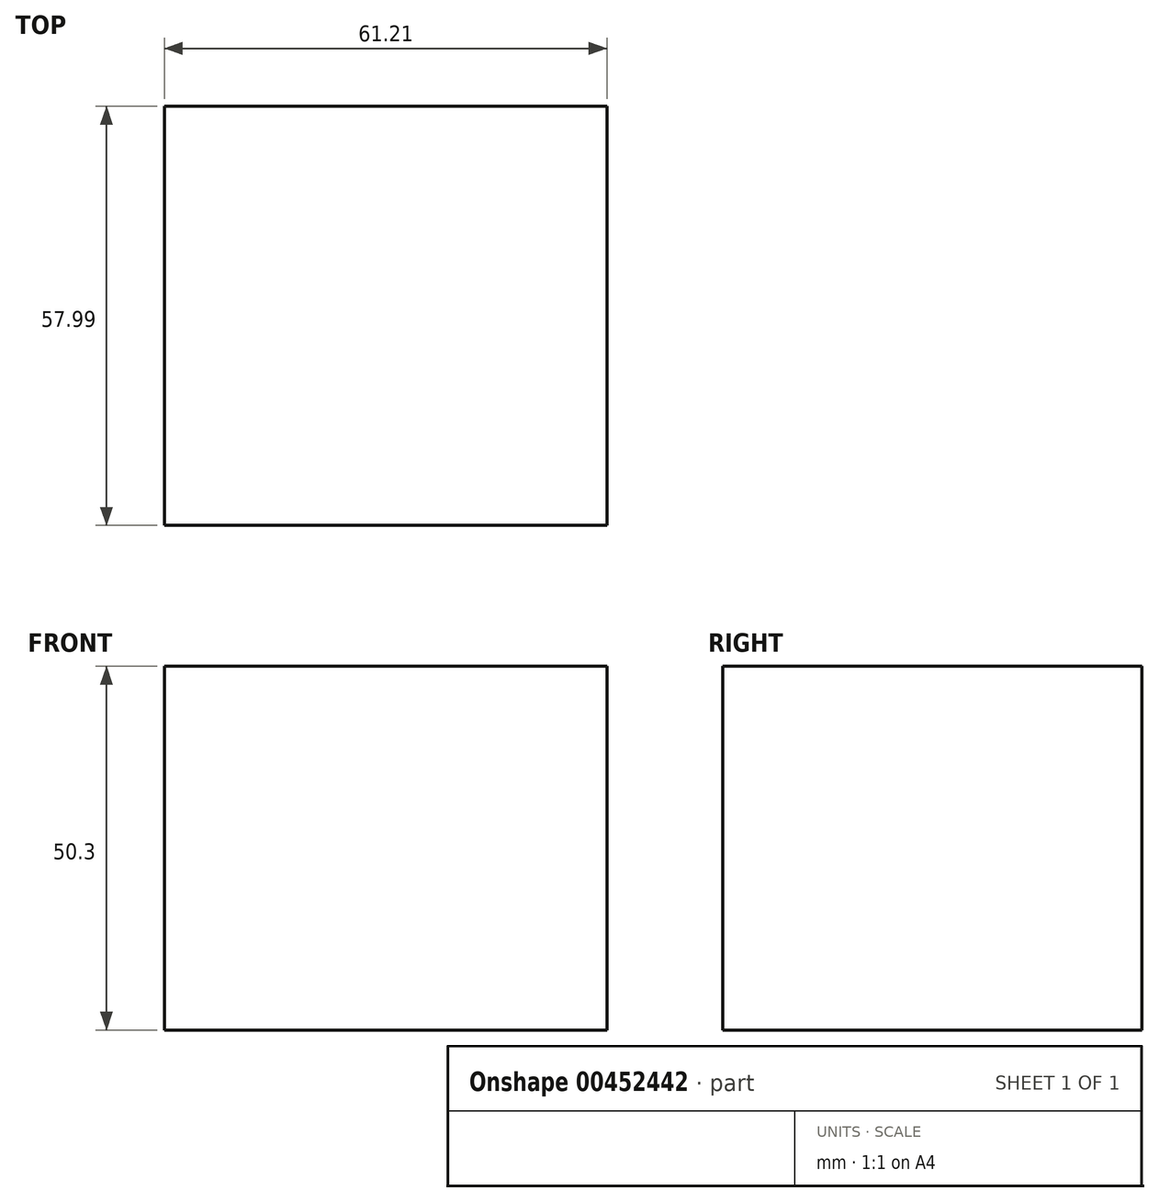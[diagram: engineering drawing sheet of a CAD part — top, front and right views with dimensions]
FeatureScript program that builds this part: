
annotation { "Feature Type Name" : "Feature", "Feature Type Description" : "" }
export const myFeature = defineFeature(function(context is Context, id is Id, definition is map)
    precondition{}
    {
        {
            var Q0;
            Q0=qCreatedBy(makeId("Right.planeOp"),FACE);
            var sketch = newSketch(context, id + "F0", { "sketchPlane" : qUnion([Q0])});
            skLineSegment(sketch, "E0.bottom", {"start": v(0, 0) * mm, "end": v(57.99, 0) * mm});
            skLineSegment(sketch, "E0.top", {"start": v(0, -50.3) * mm, "end": v(57.99, -50.3) * mm});
            skLineSegment(sketch, "E0.left", {"start": v(0, 0) * mm, "end": v(0, -50.3) * mm});
            skLineSegment(sketch, "E0.right", {"start": v(57.99, 0) * mm, "end": v(57.99, -50.3) * mm});
            skSolve(sketch);
        }
        {
            var Q0;
            Q0=makeQuery(id+"F0.imprint","IMPRINT",FACE,{"disambiguationData":[TD([[makeQuery(id+"F0.imprint","IMPRINT",EDGE,{"derivedFrom":sQuery(id+"F0.wireOp",EDGE,"E0.bottom")}),-1.0]])]});
            extrude(context, id + "F1", {"entities" : qUnion([Q0]), "depth" : 61.2 * mm});
        }
    });
